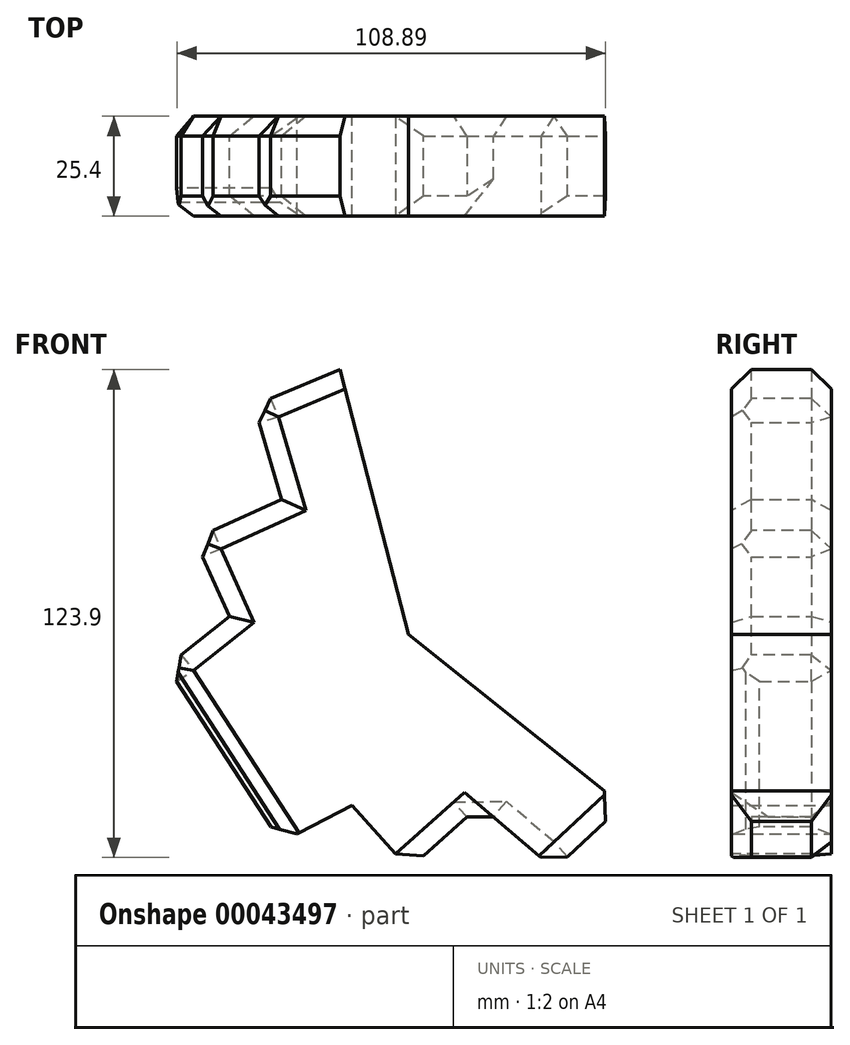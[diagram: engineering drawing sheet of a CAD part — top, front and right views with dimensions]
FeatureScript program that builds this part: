
annotation { "Feature Type Name" : "Feature", "Feature Type Description" : "" }
export const myFeature = defineFeature(function(context is Context, id is Id, definition is map)
    precondition{}
    {
        {
            var Q0;
            Q0=qCreatedBy(makeId("Front.planeOp"),FACE);
            var sketch = newSketch(context, id + "F0", { "sketchPlane" : qUnion([Q0])});
            skLineSegment(sketch, "E0", {"start": v(0, 43.41) * mm, "end": v(-46.88, 13.04) * mm});
            skLineSegment(sketch, "E1", {"start": v(-46.88, 13.04) * mm, "end": v(-32.38, -9.34) * mm});
            skLineSegment(sketch, "E2", {"start": v(-32.38, -9.34) * mm, "end": v(-14.35, 0) * mm});
            skLineSegment(sketch, "E3", {"start": v(-14.35, 0) * mm, "end": v(0, -16.15) * mm});
            skLineSegment(sketch, "E4", {"start": v(0, -16.15) * mm, "end": v(18.16, 0) * mm});
            skLineSegment(sketch, "E5", {"start": v(18.16, 0) * mm, "end": v(37.07, -16.15) * mm});
            skLineSegment(sketch, "E6", {"start": v(37.07, -16.15) * mm, "end": v(54.3, 0) * mm});
            skLineSegment(sketch, "E7", {"start": v(54.3, 0) * mm, "end": v(0, 43.41) * mm});
            skLineSegment(sketch, "E8.MirrorCS", {"start": v(-46.88, 13.04) * mm, "end": v(-61.38, 35.41) * mm});
            skLineSegment(sketch, "E9.MirrorCS", {"start": v(-61.38, 35.41) * mm, "end": v(-45.49, 48.05) * mm});
            skLineSegment(sketch, "E10.MirrorCS", {"start": v(-45.49, 48.05) * mm, "end": v(-54.36, 67.75) * mm});
            skLineSegment(sketch, "E11.MirrorCS", {"start": v(-54.36, 67.75) * mm, "end": v(-32.2, 77.73) * mm});
            skLineSegment(sketch, "E12.MirrorCS", {"start": v(-32.2, 77.73) * mm, "end": v(-39.21, 101.59) * mm});
            skLineSegment(sketch, "E13.MirrorCS", {"start": v(-39.21, 101.59) * mm, "end": v(-17.44, 110.7) * mm});
            skLineSegment(sketch, "E14.MirrorCS", {"start": v(-17.44, 110.7) * mm, "end": v(0, 43.41) * mm});
            skSolve(sketch);
        }
        {
            var Q0;
            Q0 = qSketchRegion(id + "F0", true);
            extrude(context, id + "F1", {"entities" : qUnion([Q0]), "depth" : 25.4 * mm});
        }
        {
            var Q0;
            Q0=makeQuery(id+"F1.opExtrude","CAP_EDGE",EDGE,{"disambiguationData":[OSD([sQuery(id+"F0.wireOp",EDGE,"E9.MirrorCS")])],"isStart":false});
            var Q1;
            Q1=makeQuery(id+"F1.opExtrude","CAP_EDGE",EDGE,{"disambiguationData":[OSD([sQuery(id+"F0.wireOp",EDGE,"E10.MirrorCS")])],"isStart":false});
            var Q2;
            Q2=makeQuery(id+"F1.opExtrude","CAP_EDGE",EDGE,{"disambiguationData":[OSD([sQuery(id+"F0.wireOp",EDGE,"E11.MirrorCS")])],"isStart":false});
            var Q3;
            Q3=makeQuery(id+"F1.opExtrude","CAP_EDGE",EDGE,{"disambiguationData":[OSD([sQuery(id+"F0.wireOp",EDGE,"E12.MirrorCS")])],"isStart":false});
            var Q4;
            Q4=makeQuery(id+"F1.opExtrude","CAP_EDGE",EDGE,{"disambiguationData":[OSD([sQuery(id+"F0.wireOp",EDGE,"E13.MirrorCS")])],"isStart":false});
            var Q5;
            Q5=makeQuery(id+"F1.opExtrude","CAP_EDGE",EDGE,{"disambiguationData":[OSD([sQuery(id+"F0.wireOp",EDGE,"E1"),sQuery(id+"F0.wireOp",EDGE,"E8.MirrorCS")])],"isStart":false});
            var Q6;
            Q6=makeQuery(id+"F1.opExtrude","CAP_EDGE",EDGE,{"disambiguationData":[OSD([sQuery(id+"F0.wireOp",EDGE,"E2")])],"isStart":false});
            var Q7;
            Q7=makeQuery(id+"F1.opExtrude","CAP_EDGE",EDGE,{"disambiguationData":[OSD([sQuery(id+"F0.wireOp",EDGE,"E3")])],"isStart":false});
            var Q8;
            Q8=makeQuery(id+"F1.opExtrude","CAP_EDGE",EDGE,{"disambiguationData":[OSD([sQuery(id+"F0.wireOp",EDGE,"E4")])],"isStart":false});
            var Q9;
            Q9=makeQuery(id+"F1.opExtrude","CAP_EDGE",EDGE,{"disambiguationData":[OSD([sQuery(id+"F0.wireOp",EDGE,"E5")])],"isStart":false});
            var Q10;
            Q10=makeQuery(id+"F1.opExtrude","CAP_EDGE",EDGE,{"disambiguationData":[OSD([sQuery(id+"F0.wireOp",EDGE,"E6")])],"isStart":false});
            var Q11;
            Q11=makeQuery(id+"F1.opExtrude","CAP_EDGE",EDGE,{"disambiguationData":[OSD([sQuery(id+"F0.wireOp",EDGE,"E7")])],"isStart":false});
            var Q12;
            Q12=makeQuery(id+"F1.opExtrude","CAP_EDGE",EDGE,{"disambiguationData":[OSD([sQuery(id+"F0.wireOp",EDGE,"E14.MirrorCS")])],"isStart":false});
            chamfer(context, id + "F2", {"entities" : qUnion([Q0, Q1, Q2, Q3, Q4, Q5, Q6, Q7, Q8, Q9, Q10, Q11, Q12]), "width" : 5.08 * mm, "tangentPropagation" : true});
        }
        {
            var Q0;
            Q0=makeQuery(id+"F1.opExtrude","CAP_EDGE",EDGE,{"disambiguationData":[OSD([sQuery(id+"F0.wireOp",EDGE,"E14.MirrorCS")])],"isStart":true});
            var Q1;
            Q1=makeQuery(id+"F1.opExtrude","CAP_EDGE",EDGE,{"disambiguationData":[OSD([sQuery(id+"F0.wireOp",EDGE,"E13.MirrorCS")])],"isStart":true});
            var Q2;
            Q2=makeQuery(id+"F1.opExtrude","CAP_EDGE",EDGE,{"disambiguationData":[OSD([sQuery(id+"F0.wireOp",EDGE,"E12.MirrorCS")])],"isStart":true});
            var Q3;
            Q3=makeQuery(id+"F1.opExtrude","CAP_EDGE",EDGE,{"disambiguationData":[OSD([sQuery(id+"F0.wireOp",EDGE,"E11.MirrorCS")])],"isStart":true});
            var Q4;
            Q4=makeQuery(id+"F1.opExtrude","CAP_EDGE",EDGE,{"disambiguationData":[OSD([sQuery(id+"F0.wireOp",EDGE,"E10.MirrorCS")])],"isStart":true});
            var Q5;
            Q5=makeQuery(id+"F1.opExtrude","CAP_EDGE",EDGE,{"disambiguationData":[OSD([sQuery(id+"F0.wireOp",EDGE,"E9.MirrorCS")])],"isStart":true});
            var Q6;
            Q6=makeQuery(id+"F1.opExtrude","CAP_EDGE",EDGE,{"disambiguationData":[OSD([sQuery(id+"F0.wireOp",EDGE,"E7")])],"isStart":true});
            var Q7;
            Q7=makeQuery(id+"F1.opExtrude","CAP_EDGE",EDGE,{"disambiguationData":[OSD([sQuery(id+"F0.wireOp",EDGE,"E6")])],"isStart":true});
            var Q8;
            Q8=makeQuery(id+"F1.opExtrude","CAP_EDGE",EDGE,{"disambiguationData":[OSD([sQuery(id+"F0.wireOp",EDGE,"E5")])],"isStart":true});
            var Q9;
            Q9=makeQuery(id+"F1.opExtrude","CAP_EDGE",EDGE,{"disambiguationData":[OSD([sQuery(id+"F0.wireOp",EDGE,"E4")])],"isStart":true});
            var Q10;
            Q10=makeQuery(id+"F1.opExtrude","CAP_EDGE",EDGE,{"disambiguationData":[OSD([sQuery(id+"F0.wireOp",EDGE,"E3")])],"isStart":true});
            var Q11;
            Q11=makeQuery(id+"F1.opExtrude","CAP_EDGE",EDGE,{"disambiguationData":[OSD([sQuery(id+"F0.wireOp",EDGE,"E2")])],"isStart":true});
            var Q12;
            Q12=makeQuery(id+"F1.opExtrude","CAP_EDGE",EDGE,{"disambiguationData":[OSD([sQuery(id+"F0.wireOp",EDGE,"E1"),sQuery(id+"F0.wireOp",EDGE,"E8.MirrorCS")])],"isStart":true});
            var Q13;
            Q13=makeQuery(id+"F1.opExtrude","SWEPT_EDGE",EDGE,{"disambiguationData":[OSD([sQuery(id+"F0.wireOp",EDGE,"E6"),sQuery(id+"F0.wireOp",EDGE,"E7")])]});
            var Q14;
            Q14=makeQuery(id+"F1.opExtrude","SWEPT_EDGE",EDGE,{"disambiguationData":[OSD([sQuery(id+"F0.wireOp",EDGE,"E6"),sQuery(id+"F0.wireOp",EDGE,"E5")])]});
            var Q15;
            Q15=makeQuery(id+"F1.opExtrude","SWEPT_EDGE",EDGE,{"disambiguationData":[OSD([sQuery(id+"F0.wireOp",EDGE,"E4"),sQuery(id+"F0.wireOp",EDGE,"E3")])]});
            var Q16;
            Q16=makeQuery(id+"F1.opExtrude","SWEPT_FACE",FACE,{"disambiguationData":[OSD([sQuery(id+"F0.wireOp",EDGE,"E1"),sQuery(id+"F0.wireOp",EDGE,"E8.MirrorCS")])]});
            var Q17;
            Q17=makeQuery(id+"F1.opExtrude","SWEPT_EDGE",EDGE,{"disambiguationData":[OSD([sQuery(id+"F0.wireOp",EDGE,"E10.MirrorCS"),sQuery(id+"F0.wireOp",EDGE,"E11.MirrorCS")])]});
            var Q18;
            Q18=makeQuery(id+"F1.opExtrude","SWEPT_EDGE",EDGE,{"disambiguationData":[OSD([sQuery(id+"F0.wireOp",EDGE,"E12.MirrorCS"),sQuery(id+"F0.wireOp",EDGE,"E13.MirrorCS")])]});
            var Q19;
            {var subQ0=sQuery(id+"F0.wireOp",EDGE,"E14.MirrorCS");Q19=makeQuery(id+"F2.opChamfer","BLEND_EDGE",EDGE,{"blendedFrom":[makeQuery(id+"F1.opExtrude","CAP_EDGE",EDGE,{"disambiguationData":[OSD([subQ0])],"isStart":false}),makeQuery(id+"F1.opExtrude","SWEPT_FACE",FACE,{"disambiguationData":[OSD([subQ0])]})],"blendedInto":[makeQuery(id+"F1.opExtrude","SWEPT_FACE",FACE,{"disambiguationData":[OSD([subQ0])]})]});}
            var Q20;
            {var subQ0=sQuery(id+"F0.wireOp",EDGE,"E7");Q20=makeQuery(id+"F2.opChamfer","BLEND_EDGE",EDGE,{"blendedFrom":[makeQuery(id+"F1.opExtrude","CAP_EDGE",EDGE,{"disambiguationData":[OSD([subQ0])],"isStart":false}),makeQuery(id+"F1.opExtrude","SWEPT_FACE",FACE,{"disambiguationData":[OSD([subQ0])]})],"blendedInto":[makeQuery(id+"F1.opExtrude","SWEPT_FACE",FACE,{"disambiguationData":[OSD([subQ0])]})]});}
            chamfer(context, id + "F3", {"entities" : qUnion([Q0, Q1, Q2, Q3, Q4, Q5, Q6, Q7, Q8, Q9, Q10, Q11, Q12, Q13, Q14, Q15, Q16, Q17, Q18, Q19, Q20]), "width" : 5.08 * mm, "tangentPropagation" : true});
        }
    });
